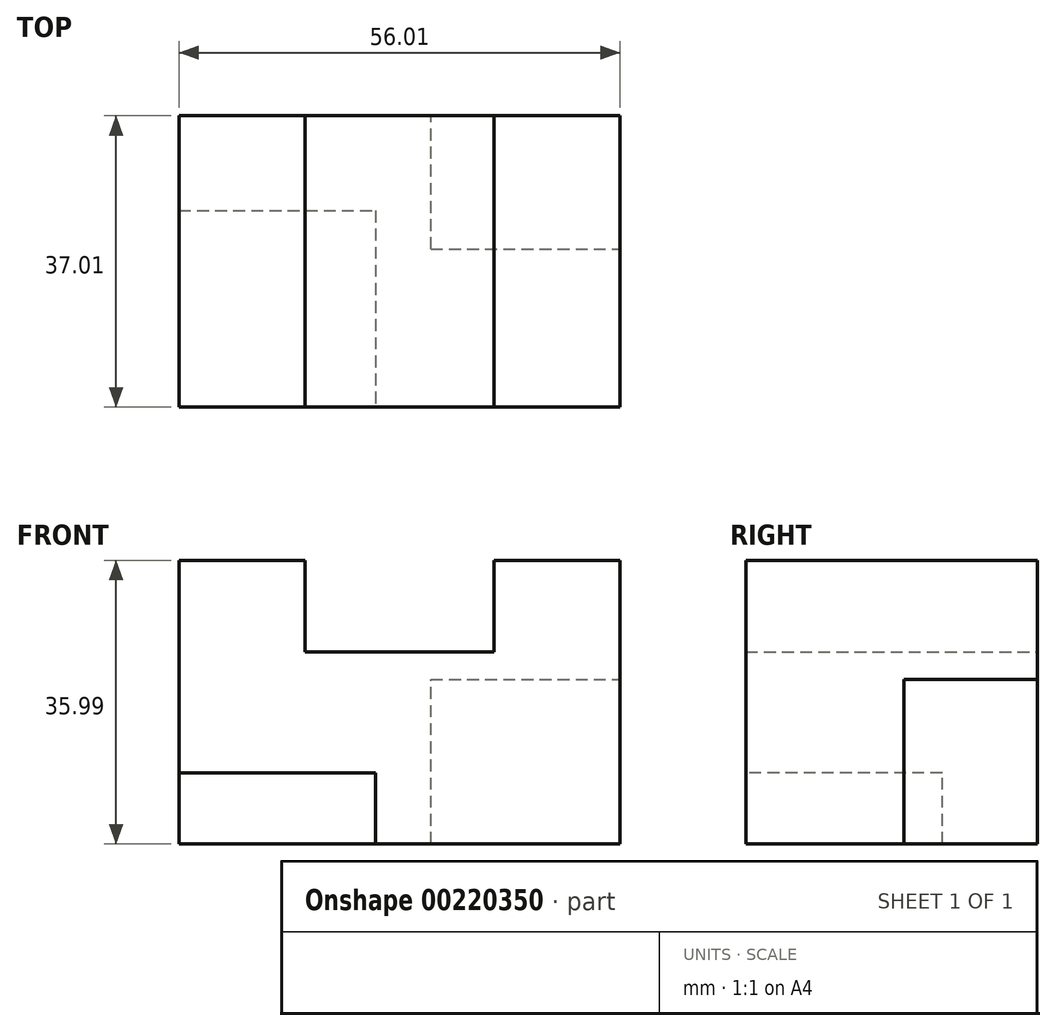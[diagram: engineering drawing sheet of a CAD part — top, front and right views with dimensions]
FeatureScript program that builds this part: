
annotation { "Feature Type Name" : "Feature", "Feature Type Description" : "" }
export const myFeature = defineFeature(function(context is Context, id is Id, definition is map)
    precondition{}
    {
        {
            var Q0;
            Q0=qCreatedBy(makeId("Front.planeOp"),FACE);
            var sketch = newSketch(context, id + "F0", { "sketchPlane" : qUnion([Q0])});
            skLineSegment(sketch, "E0.bottom", {"start": v(0, 0) * mm, "end": v(56, 0) * mm});
            skLineSegment(sketch, "E0.top", {"start": v(0, 36) * mm, "end": v(16, 36) * mm});
            skLineSegment(sketch, "E0.left", {"start": v(0, 0) * mm, "end": v(0, 36) * mm});
            skLineSegment(sketch, "E0.right", {"start": v(56, 0) * mm, "end": v(56, 36) * mm});
            skLineSegment(sketch, "E1.0", {"start": v(16, 24.38) * mm, "end": v(16, 36) * mm});
            skLineSegment(sketch, "E2.0", {"start": v(40, 24.38) * mm, "end": v(40, 36) * mm});
            skLineSegment(sketch, "E3.0", {"start": v(16, 24.38) * mm, "end": v(40, 24.38) * mm});
            skLineSegment(sketch, "E4.trimOffspring", {"start": v(40, 36) * mm, "end": v(56, 36) * mm});
            skSolve(sketch);
        }
        {
            var Q0;
            Q0=makeQuery(id+"F0.imprint","IMPRINT",FACE,{"disambiguationData":[TD([[makeQuery(id+"F0.imprint","IMPRINT",EDGE,{"derivedFrom":sQuery(id+"F0.wireOp",EDGE,"E0.bottom")}),1.0]])]});
            extrude(context, id + "F1", {"entities" : qUnion([Q0]), "depth" : 37 * mm});
        }
        {
            var Q0;
            Q0=makeQuery(id+"F1.opExtrude","CAP_FACE",FACE,{"disambiguationData":[OSD([sQuery(id+"F0.wireOp",EDGE,"E0.bottom"),sQuery(id+"F0.wireOp",EDGE,"E0.top"),sQuery(id+"F0.wireOp",EDGE,"E0.left"),sQuery(id+"F0.wireOp",EDGE,"E0.right"),sQuery(id+"F0.wireOp",EDGE,"E1.0"),sQuery(id+"F0.wireOp",EDGE,"E2.0"),sQuery(id+"F0.wireOp",EDGE,"E3.0"),sQuery(id+"F0.wireOp",EDGE,"E4.trimOffspring")])],"isStart":false});
            var sketch = newSketch(context, id + "F2", { "sketchPlane" : qUnion([Q0])});
            skLineSegment(sketch, "E5.bottom", {"start": v(0, 0) * mm, "end": v(24.97, 0) * mm});
            skLineSegment(sketch, "E5.top", {"start": v(0, 9) * mm, "end": v(24.97, 9) * mm});
            skLineSegment(sketch, "E5.left", {"start": v(0, 0) * mm, "end": v(0, 9) * mm});
            skLineSegment(sketch, "E5.right", {"start": v(24.97, 0) * mm, "end": v(24.97, 9) * mm});
            skSolve(sketch);
        }
        {
            var Q0;
            Q0=makeQuery(id+"F2.imprint","IMPRINT",FACE,{"disambiguationData":[TD([[makeQuery(id+"F2.imprint","IMPRINT",EDGE,{"derivedFrom":sQuery(id+"F2.wireOp",EDGE,"E5.bottom")}),1.0]])]});
            extrude(context, id + "F3", {"entities" : qUnion([Q0]), "operationType" : NewBodyOperationType.REMOVE, "oppositeDirection" : true, "depth" : 24.94 * mm});
        }
        {
            var Q0;
            Q0=makeQuery(id+"F1.opExtrude","SWEPT_FACE",FACE,{"disambiguationData":[OSD([sQuery(id+"F0.wireOp",EDGE,"E0.right")])]});
            var sketch = newSketch(context, id + "F4", { "sketchPlane" : qUnion([Q0])});
            skLineSegment(sketch, "E6.bottom", {"start": v(0, 0) * mm, "end": v(-16.94, 0) * mm});
            skLineSegment(sketch, "E6.top", {"start": v(0, 20.85) * mm, "end": v(-16.94, 20.85) * mm});
            skLineSegment(sketch, "E6.left", {"start": v(0, 0) * mm, "end": v(0, 20.85) * mm});
            skLineSegment(sketch, "E6.right", {"start": v(-16.94, 0) * mm, "end": v(-16.94, 20.85) * mm});
            skSolve(sketch);
        }
        {
            var Q0;
            Q0=makeQuery(id+"F4.imprint","IMPRINT",FACE,{"disambiguationData":[TD([[makeQuery(id+"F4.imprint","IMPRINT",EDGE,{"derivedFrom":sQuery(id+"F4.wireOp",EDGE,"E6.bottom")}),1.0]])]});
            extrude(context, id + "F5", {"entities" : qUnion([Q0]), "operationType" : NewBodyOperationType.REMOVE, "oppositeDirection" : true, "depth" : 24 * mm});
        }
    });
